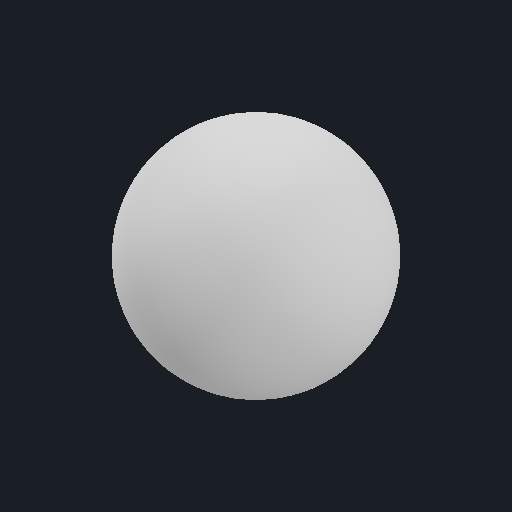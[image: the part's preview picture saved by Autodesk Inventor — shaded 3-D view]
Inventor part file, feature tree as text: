
AUTODESK INVENTOR PART (.ipt)
format: ipt  version: 2024.1 (Build 281209000, 209)  size: 122,880 bytes
history: native  units: in
note: dims shown in document units (in); Inventor stores cm internally (conversion verified against a paired STEP export)
features: revolve x1
ambient origin geometry x8: Origin, YZ Plane, XZ Plane, XY Plane, X Axis, Y Axis, Z Axis, Center Point
bodies: Solid1 (feature_tree)
feature tree (1):
  revolve  "Revolve1"  [1 undecoded]
note: 1 required parameter value undecoded (feature->parameter linkage not recoverable at this tier; creation-order binding heuristic only, values carry confidence <= 0.55)
